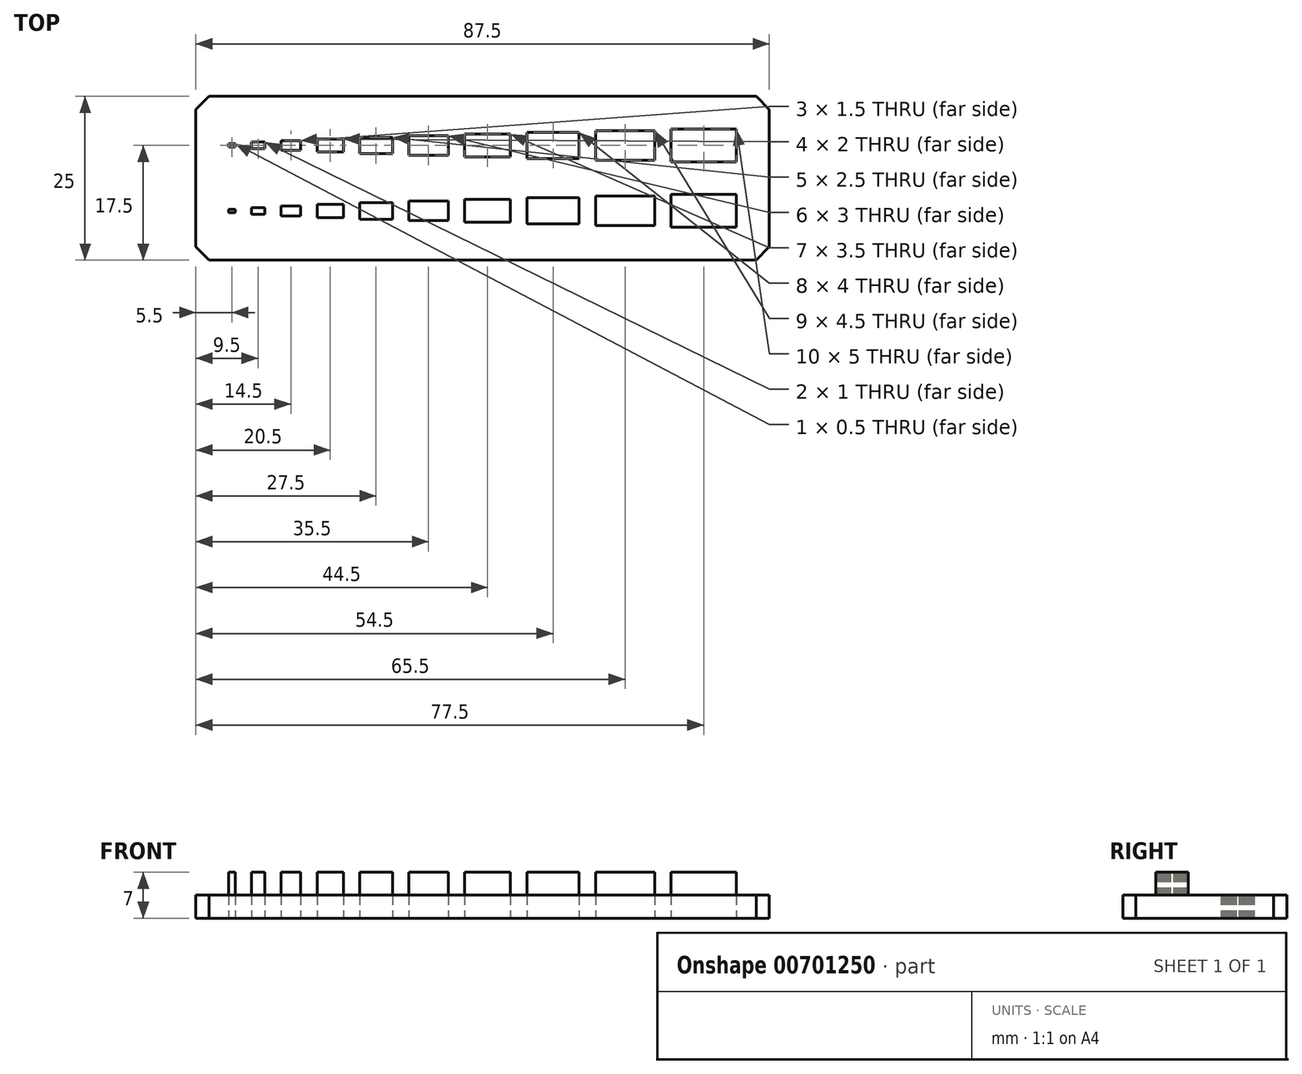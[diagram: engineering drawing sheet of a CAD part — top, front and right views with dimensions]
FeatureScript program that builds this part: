
annotation { "Feature Type Name" : "Feature", "Feature Type Description" : "" }
export const myFeature = defineFeature(function(context is Context, id is Id, definition is map)
    precondition{}
    {
        {
            var Q0;
            Q0=qCreatedBy(makeId("Top.planeOp"),FACE);
            var sketch = newSketch(context, id + "F0", { "sketchPlane" : qUnion([Q0])});
            skLineSegment(sketch, "E0.bottom", {"start": v(-37.75, 5.25) * mm, "end": v(-38.25, 5.25) * mm});
            skLineSegment(sketch, "E0.top", {"start": v(-37.75, 4.75) * mm, "end": v(-38.75, 4.75) * mm});
            skLineSegment(sketch, "E0.left", {"start": v(-37.75, 5.25) * mm, "end": v(-37.75, 4.75) * mm});
            skLineSegment(sketch, "E0.right", {"start": v(-38.75, 5.25) * mm, "end": v(-38.75, 4.75) * mm});
            skPoint(sketch, "E0.middle", {"position": v(-38.25, 5) * mm});
            skPoint(sketch, "E1", {"position": v(-38.25, 5.25) * mm});
            skLineSegment(sketch, "E2", {"start": v(-38.25, 5.25) * mm, "end": v(-38.75, 5.25) * mm});
            skLineSegment(sketch, "E3.bottom", {"start": v(-33.25, 5.5) * mm, "end": v(-34.25, 5.5) * mm});
            skLineSegment(sketch, "E3.top", {"start": v(-33.25, 4.5) * mm, "end": v(-35.25, 4.5) * mm});
            skLineSegment(sketch, "E3.left", {"start": v(-33.25, 5.5) * mm, "end": v(-33.25, 4.5) * mm});
            skLineSegment(sketch, "E3.right", {"start": v(-35.25, 5.5) * mm, "end": v(-35.25, 4.5) * mm});
            skPoint(sketch, "E3.middle", {"position": v(-34.25, 5) * mm});
            skLineSegment(sketch, "E4", {"start": v(-34.25, 5.5) * mm, "end": v(-35.25, 5.5) * mm});
            skLineSegment(sketch, "E5", {"start": v(-37.75, 5) * mm, "end": v(-35.25, 5) * mm, "construction": true});
            skLineSegment(sketch, "E6", {"start": v(-33.25, 5) * mm, "end": v(-30.75, 5) * mm, "construction": true});
            skLineSegment(sketch, "E7.bottom", {"start": v(-30.75, 5.75) * mm, "end": v(-29.25, 5.75) * mm});
            skLineSegment(sketch, "E7.top", {"start": v(-30.75, 4.25) * mm, "end": v(-27.75, 4.25) * mm});
            skLineSegment(sketch, "E7.left", {"start": v(-30.75, 5.75) * mm, "end": v(-30.75, 4.25) * mm});
            skLineSegment(sketch, "E7.right", {"start": v(-27.75, 5.75) * mm, "end": v(-27.75, 4.25) * mm});
            skPoint(sketch, "E7.middle", {"position": v(-29.25, 5) * mm});
            skLineSegment(sketch, "E8", {"start": v(-29.25, 5.75) * mm, "end": v(-27.75, 5.75) * mm});
            skLineSegment(sketch, "E9", {"start": v(-27.75, 5) * mm, "end": v(-25.25, 5) * mm, "construction": true});
            skLineSegment(sketch, "E10.bottom", {"start": v(-25.25, 6) * mm, "end": v(-23.25, 6) * mm});
            skLineSegment(sketch, "E10.top", {"start": v(-25.25, 4) * mm, "end": v(-21.25, 4) * mm});
            skLineSegment(sketch, "E10.left", {"start": v(-25.25, 6) * mm, "end": v(-25.25, 4) * mm});
            skLineSegment(sketch, "E10.right", {"start": v(-21.25, 6) * mm, "end": v(-21.25, 4) * mm});
            skPoint(sketch, "E10.middle", {"position": v(-23.25, 5) * mm});
            skLineSegment(sketch, "E11", {"start": v(-23.25, 6) * mm, "end": v(-21.25, 6) * mm});
            skLineSegment(sketch, "E12", {"start": v(-21.25, 5) * mm, "end": v(-18.75, 5) * mm, "construction": true});
            skLineSegment(sketch, "E13.bottom", {"start": v(-18.75, 6.25) * mm, "end": v(-16.25, 6.25) * mm});
            skLineSegment(sketch, "E13.top", {"start": v(-18.75, 3.75) * mm, "end": v(-13.75, 3.75) * mm});
            skLineSegment(sketch, "E13.left", {"start": v(-18.75, 6.25) * mm, "end": v(-18.75, 3.75) * mm});
            skLineSegment(sketch, "E13.right", {"start": v(-13.75, 6.25) * mm, "end": v(-13.75, 3.75) * mm});
            skPoint(sketch, "E13.middle", {"position": v(-16.25, 5) * mm});
            skLineSegment(sketch, "E14", {"start": v(-16.25, 6.25) * mm, "end": v(-13.75, 6.25) * mm});
            skLineSegment(sketch, "E15", {"start": v(-13.75, 5) * mm, "end": v(-11.25, 5) * mm, "construction": true});
            skPoint(sketch, "E15.startSnap0", {"position": v(-13.75, 5) * mm});
            skLineSegment(sketch, "E16.bottom", {"start": v(-11.25, 6.5) * mm, "end": v(-8.25, 6.5) * mm});
            skLineSegment(sketch, "E16.top", {"start": v(-11.25, 3.5) * mm, "end": v(-5.25, 3.5) * mm});
            skLineSegment(sketch, "E16.left", {"start": v(-11.25, 6.5) * mm, "end": v(-11.25, 3.5) * mm});
            skLineSegment(sketch, "E16.right", {"start": v(-5.25, 6.5) * mm, "end": v(-5.25, 3.5) * mm});
            skPoint(sketch, "E16.middle", {"position": v(-8.25, 5) * mm});
            skLineSegment(sketch, "E17", {"start": v(-8.25, 6.5) * mm, "end": v(-5.25, 6.5) * mm});
            skLineSegment(sketch, "E18", {"start": v(-5.25, 5) * mm, "end": v(-2.75, 5) * mm, "construction": true});
            skLineSegment(sketch, "E19.bottom", {"start": v(-2.75, 6.75) * mm, "end": v(0.75, 6.75) * mm});
            skLineSegment(sketch, "E19.top", {"start": v(-2.75, 3.25) * mm, "end": v(4.25, 3.25) * mm});
            skLineSegment(sketch, "E19.left", {"start": v(-2.75, 6.75) * mm, "end": v(-2.75, 3.25) * mm});
            skLineSegment(sketch, "E19.right", {"start": v(4.25, 6.75) * mm, "end": v(4.25, 3.25) * mm});
            skPoint(sketch, "E19.middle", {"position": v(0.75, 5) * mm});
            skLineSegment(sketch, "E20", {"start": v(0.75, 6.75) * mm, "end": v(4.25, 6.75) * mm});
            skLineSegment(sketch, "E21", {"start": v(4.25, 5) * mm, "end": v(6.75, 5) * mm, "construction": true});
            skLineSegment(sketch, "E22.bottom", {"start": v(6.75, 7) * mm, "end": v(10.75, 7) * mm});
            skLineSegment(sketch, "E22.top", {"start": v(6.75, 3) * mm, "end": v(14.75, 3) * mm});
            skLineSegment(sketch, "E22.left", {"start": v(6.75, 7) * mm, "end": v(6.75, 3) * mm});
            skLineSegment(sketch, "E22.right", {"start": v(14.75, 7) * mm, "end": v(14.75, 3) * mm});
            skPoint(sketch, "E22.middle", {"position": v(10.75, 5) * mm});
            skLineSegment(sketch, "E23", {"start": v(10.75, 7) * mm, "end": v(14.75, 7) * mm});
            skLineSegment(sketch, "E24", {"start": v(14.75, 5) * mm, "end": v(17.25, 5) * mm, "construction": true});
            skLineSegment(sketch, "E25.bottom", {"start": v(17.25, 7.25) * mm, "end": v(21.75, 7.25) * mm});
            skLineSegment(sketch, "E25.top", {"start": v(17.25, 2.75) * mm, "end": v(26.25, 2.75) * mm});
            skLineSegment(sketch, "E25.left", {"start": v(17.25, 7.25) * mm, "end": v(17.25, 2.75) * mm});
            skLineSegment(sketch, "E25.right", {"start": v(26.25, 7.25) * mm, "end": v(26.25, 2.75) * mm});
            skPoint(sketch, "E25.middle", {"position": v(21.75, 5) * mm});
            skLineSegment(sketch, "E26", {"start": v(21.75, 7.25) * mm, "end": v(26.25, 7.25) * mm});
            skLineSegment(sketch, "E27", {"start": v(26.25, 5) * mm, "end": v(28.75, 5) * mm, "construction": true});
            skLineSegment(sketch, "E28.bottom", {"start": v(28.75, 7.5) * mm, "end": v(33.75, 7.5) * mm});
            skLineSegment(sketch, "E28.top", {"start": v(28.75, 2.5) * mm, "end": v(38.75, 2.5) * mm});
            skLineSegment(sketch, "E28.left", {"start": v(28.75, 7.5) * mm, "end": v(28.75, 2.5) * mm});
            skLineSegment(sketch, "E28.right", {"start": v(38.75, 7.5) * mm, "end": v(38.75, 2.5) * mm});
            skPoint(sketch, "E28.middle", {"position": v(33.75, 5) * mm});
            skLineSegment(sketch, "E29", {"start": v(33.75, 7.5) * mm, "end": v(38.75, 7.5) * mm});
            skLineSegment(sketch, "E30", {"start": v(38.75, 5) * mm, "end": v(43.75, 5) * mm, "construction": true});
            skLineSegment(sketch, "E31", {"start": v(-38.75, 5) * mm, "end": v(-43.75, 5) * mm, "construction": true});
            skLineSegment(sketch, "E32.bottom", {"start": v(43.75, 12.5) * mm, "end": v(-43.75, 12.5) * mm});
            skLineSegment(sketch, "E32.top", {"start": v(43.75, -12.5) * mm, "end": v(-43.75, -12.5) * mm});
            skLineSegment(sketch, "E32.left", {"start": v(43.75, 12.5) * mm, "end": v(43.75, -12.5) * mm});
            skLineSegment(sketch, "E32.right", {"start": v(-43.75, 12.5) * mm, "end": v(-43.75, -12.5) * mm});
            skPoint(sketch, "E32.middle", {"position": v(0, 0) * mm});
            skLineSegment(sketch, "E33", {"start": v(0, 0) * mm, "end": v(15.69, 0) * mm, "construction": true});
            skLineSegment(sketch, "E34.MirrorCS", {"start": v(-11.25, -6.5) * mm, "end": v(-11.25, -3.5) * mm});
            skLineSegment(sketch, "E35.MirrorCS", {"start": v(-13.75, -6.25) * mm, "end": v(-13.75, -3.75) * mm});
            skLineSegment(sketch, "E36.MirrorCS", {"start": v(-5.25, -6.5) * mm, "end": v(-5.25, -3.5) * mm});
            skLineSegment(sketch, "E37.MirrorCS", {"start": v(-11.25, -3.5) * mm, "end": v(-5.25, -3.5) * mm});
            skLineSegment(sketch, "E38.MirrorCS", {"start": v(-2.75, -6.75) * mm, "end": v(-2.75, -3.25) * mm});
            skLineSegment(sketch, "E39.MirrorCS", {"start": v(4.25, -6.75) * mm, "end": v(4.25, -3.25) * mm});
            skLineSegment(sketch, "E40.MirrorCS", {"start": v(28.75, -2.5) * mm, "end": v(38.75, -2.5) * mm});
            skLineSegment(sketch, "E41.MirrorCS", {"start": v(26.25, -7.25) * mm, "end": v(26.25, -2.75) * mm});
            skLineSegment(sketch, "E42.MirrorCS", {"start": v(-2.75, -3.25) * mm, "end": v(4.25, -3.25) * mm});
            skLineSegment(sketch, "E43.MirrorCS", {"start": v(28.75, -7.5) * mm, "end": v(28.75, -2.5) * mm});
            skLineSegment(sketch, "E44.MirrorCS", {"start": v(6.75, -3) * mm, "end": v(14.75, -3) * mm});
            skLineSegment(sketch, "E45.MirrorCS", {"start": v(17.25, -2.75) * mm, "end": v(26.25, -2.75) * mm});
            skLineSegment(sketch, "E46.MirrorCS", {"start": v(14.75, -7) * mm, "end": v(14.75, -3) * mm});
            skLineSegment(sketch, "E47.MirrorCS", {"start": v(38.75, -7.5) * mm, "end": v(38.75, -2.5) * mm});
            skLineSegment(sketch, "E48.MirrorCS", {"start": v(6.75, -7) * mm, "end": v(6.75, -3) * mm});
            skLineSegment(sketch, "E49.MirrorCS", {"start": v(17.25, -7.25) * mm, "end": v(17.25, -2.75) * mm});
            skLineSegment(sketch, "E50.MirrorCS", {"start": v(-30.75, -5.75) * mm, "end": v(-30.75, -4.25) * mm});
            skLineSegment(sketch, "E51.MirrorCS", {"start": v(-33.25, -5.5) * mm, "end": v(-33.25, -4.5) * mm});
            skLineSegment(sketch, "E52.MirrorCS", {"start": v(-27.75, -5.75) * mm, "end": v(-27.75, -4.25) * mm});
            skLineSegment(sketch, "E53.MirrorCS", {"start": v(-35.25, -5.5) * mm, "end": v(-35.25, -4.5) * mm});
            skLineSegment(sketch, "E54.MirrorCS", {"start": v(-30.75, -4.25) * mm, "end": v(-27.75, -4.25) * mm});
            skLineSegment(sketch, "E55.MirrorCS", {"start": v(-25.25, -6) * mm, "end": v(-25.25, -4) * mm});
            skLineSegment(sketch, "E56.MirrorCS", {"start": v(-18.75, -6.25) * mm, "end": v(-18.75, -3.75) * mm});
            skLineSegment(sketch, "E57.MirrorCS", {"start": v(-18.75, -3.75) * mm, "end": v(-13.75, -3.75) * mm});
            skLineSegment(sketch, "E58.MirrorCS", {"start": v(-33.25, -4.5) * mm, "end": v(-35.25, -4.5) * mm});
            skLineSegment(sketch, "E59.MirrorCS", {"start": v(-25.25, -4) * mm, "end": v(-21.25, -4) * mm});
            skLineSegment(sketch, "E60.MirrorCS", {"start": v(-21.25, -6) * mm, "end": v(-21.25, -4) * mm});
            skLineSegment(sketch, "E61.MirrorCS", {"start": v(-38.75, -5.25) * mm, "end": v(-38.75, -4.75) * mm});
            skLineSegment(sketch, "E62.MirrorCS", {"start": v(-37.75, -4.75) * mm, "end": v(-38.75, -4.75) * mm});
            skLineSegment(sketch, "E63.MirrorCS", {"start": v(-37.75, -5.25) * mm, "end": v(-37.75, -4.75) * mm});
            skLineSegment(sketch, "E64", {"start": v(-38.75, -5.25) * mm, "end": v(-37.75, -5.25) * mm});
            skLineSegment(sketch, "E65", {"start": v(-35.25, -5.5) * mm, "end": v(-33.25, -5.5) * mm});
            skLineSegment(sketch, "E66", {"start": v(-30.75, -5.75) * mm, "end": v(-27.75, -5.75) * mm});
            skLineSegment(sketch, "E67", {"start": v(-25.25, -6) * mm, "end": v(-21.25, -6) * mm});
            skLineSegment(sketch, "E68", {"start": v(-18.75, -6.25) * mm, "end": v(-13.75, -6.25) * mm});
            skLineSegment(sketch, "E69", {"start": v(-11.25, -6.5) * mm, "end": v(-5.25, -6.5) * mm});
            skLineSegment(sketch, "E70", {"start": v(-2.75, -6.75) * mm, "end": v(4.25, -6.75) * mm});
            skLineSegment(sketch, "E71", {"start": v(6.75, -7) * mm, "end": v(14.75, -7) * mm});
            skLineSegment(sketch, "E72", {"start": v(17.25, -7.25) * mm, "end": v(26.25, -7.25) * mm});
            skLineSegment(sketch, "E73", {"start": v(28.75, -7.5) * mm, "end": v(38.75, -7.5) * mm});
            skLineSegment(sketch, "E74", {"start": v(33.75, 7.5) * mm, "end": v(33.75, 12.5) * mm, "construction": true});
            skSolve(sketch);
        }
        {
            var Q0;
            Q0=qSketchRegion(id+"F0",true);
            extrude(context, id + "F1", {"entities" : qUnion([Q0]), "depth" : 3.5 * mm, "offsetDistance" : 25 * mm});
        }
        {
            var Q0;
            Q0=makeQuery(id+"F0.imprint","IMPRINT",FACE,{"disambiguationData":[TD([[makeQuery(id+"F0.imprint","IMPRINT",EDGE,{"derivedFrom":sQuery(id+"F0.wireOp",EDGE,"E61.MirrorCS")}),-1.0]])]});
            var Q1;
            Q1=makeQuery(id+"F0.imprint","IMPRINT",FACE,{"disambiguationData":[TD([[makeQuery(id+"F0.imprint","IMPRINT",EDGE,{"derivedFrom":sQuery(id+"F0.wireOp",EDGE,"E51.MirrorCS")}),1.0]])]});
            var Q2;
            Q2=makeQuery(id+"F0.imprint","IMPRINT",FACE,{"disambiguationData":[TD([[makeQuery(id+"F0.imprint","IMPRINT",EDGE,{"derivedFrom":sQuery(id+"F0.wireOp",EDGE,"E50.MirrorCS")}),-1.0]])]});
            var Q3;
            Q3=makeQuery(id+"F0.imprint","IMPRINT",FACE,{"disambiguationData":[TD([[makeQuery(id+"F0.imprint","IMPRINT",EDGE,{"derivedFrom":sQuery(id+"F0.wireOp",EDGE,"E55.MirrorCS")}),-1.0]])]});
            var Q4;
            Q4=makeQuery(id+"F0.imprint","IMPRINT",FACE,{"disambiguationData":[TD([[makeQuery(id+"F0.imprint","IMPRINT",EDGE,{"derivedFrom":sQuery(id+"F0.wireOp",EDGE,"E35.MirrorCS")}),1.0]])]});
            var Q5;
            Q5=makeQuery(id+"F0.imprint","IMPRINT",FACE,{"disambiguationData":[TD([[makeQuery(id+"F0.imprint","IMPRINT",EDGE,{"derivedFrom":sQuery(id+"F0.wireOp",EDGE,"E34.MirrorCS")}),-1.0]])]});
            var Q6;
            Q6=makeQuery(id+"F0.imprint","IMPRINT",FACE,{"disambiguationData":[TD([[makeQuery(id+"F0.imprint","IMPRINT",EDGE,{"derivedFrom":sQuery(id+"F0.wireOp",EDGE,"E38.MirrorCS")}),-1.0]])]});
            var Q7;
            Q7=makeQuery(id+"F0.imprint","IMPRINT",FACE,{"disambiguationData":[TD([[makeQuery(id+"F0.imprint","IMPRINT",EDGE,{"derivedFrom":sQuery(id+"F0.wireOp",EDGE,"E44.MirrorCS")}),-1.0]])]});
            var Q8;
            Q8=makeQuery(id+"F0.imprint","IMPRINT",FACE,{"disambiguationData":[TD([[makeQuery(id+"F0.imprint","IMPRINT",EDGE,{"derivedFrom":sQuery(id+"F0.wireOp",EDGE,"E41.MirrorCS")}),1.0]])]});
            var Q9;
            Q9=makeQuery(id+"F0.imprint","IMPRINT",FACE,{"disambiguationData":[TD([[makeQuery(id+"F0.imprint","IMPRINT",EDGE,{"derivedFrom":sQuery(id+"F0.wireOp",EDGE,"E40.MirrorCS")}),-1.0]])]});
            var Q10;
            Q10=makeQuery(id+"F1.opExtrude","CAP_FACE",FACE,{"disambiguationData":[OSD([sQuery(id+"F0.wireOp",EDGE,"E0.bottom"),sQuery(id+"F0.wireOp",EDGE,"E0.top"),sQuery(id+"F0.wireOp",EDGE,"E0.left"),sQuery(id+"F0.wireOp",EDGE,"E0.right"),sQuery(id+"F0.wireOp",EDGE,"E2"),sQuery(id+"F0.wireOp",EDGE,"E3.bottom"),sQuery(id+"F0.wireOp",EDGE,"E3.top"),sQuery(id+"F0.wireOp",EDGE,"E3.left"),sQuery(id+"F0.wireOp",EDGE,"E3.right"),sQuery(id+"F0.wireOp",EDGE,"E4"),sQuery(id+"F0.wireOp",EDGE,"E7.bottom"),sQuery(id+"F0.wireOp",EDGE,"E7.top"),sQuery(id+"F0.wireOp",EDGE,"E7.left"),sQuery(id+"F0.wireOp",EDGE,"E7.right"),sQuery(id+"F0.wireOp",EDGE,"E8"),sQuery(id+"F0.wireOp",EDGE,"E10.bottom"),sQuery(id+"F0.wireOp",EDGE,"E10.top"),sQuery(id+"F0.wireOp",EDGE,"E10.left"),sQuery(id+"F0.wireOp",EDGE,"E10.right"),sQuery(id+"F0.wireOp",EDGE,"E11"),sQuery(id+"F0.wireOp",EDGE,"E13.bottom"),sQuery(id+"F0.wireOp",EDGE,"E13.top"),sQuery(id+"F0.wireOp",EDGE,"E13.left"),sQuery(id+"F0.wireOp",EDGE,"E13.right"),sQuery(id+"F0.wireOp",EDGE,"E14"),sQuery(id+"F0.wireOp",EDGE,"E16.bottom"),sQuery(id+"F0.wireOp",EDGE,"E16.top"),sQuery(id+"F0.wireOp",EDGE,"E16.left"),sQuery(id+"F0.wireOp",EDGE,"E16.right"),sQuery(id+"F0.wireOp",EDGE,"E17"),sQuery(id+"F0.wireOp",EDGE,"E19.bottom"),sQuery(id+"F0.wireOp",EDGE,"E19.top"),sQuery(id+"F0.wireOp",EDGE,"E19.left"),sQuery(id+"F0.wireOp",EDGE,"E19.right"),sQuery(id+"F0.wireOp",EDGE,"E20"),sQuery(id+"F0.wireOp",EDGE,"E22.bottom"),sQuery(id+"F0.wireOp",EDGE,"E22.top"),sQuery(id+"F0.wireOp",EDGE,"E22.left"),sQuery(id+"F0.wireOp",EDGE,"E22.right"),sQuery(id+"F0.wireOp",EDGE,"E23"),sQuery(id+"F0.wireOp",EDGE,"E25.bottom"),sQuery(id+"F0.wireOp",EDGE,"E25.top"),sQuery(id+"F0.wireOp",EDGE,"E25.left"),sQuery(id+"F0.wireOp",EDGE,"E25.right"),sQuery(id+"F0.wireOp",EDGE,"E26"),sQuery(id+"F0.wireOp",EDGE,"E28.bottom"),sQuery(id+"F0.wireOp",EDGE,"E28.top"),sQuery(id+"F0.wireOp",EDGE,"E28.left"),sQuery(id+"F0.wireOp",EDGE,"E28.right"),sQuery(id+"F0.wireOp",EDGE,"E29"),sQuery(id+"F0.wireOp",EDGE,"E32.bottom"),sQuery(id+"F0.wireOp",EDGE,"E32.top"),sQuery(id+"F0.wireOp",EDGE,"E32.left"),sQuery(id+"F0.wireOp",EDGE,"E32.right"),sQuery(id+"F0.wireOp",EDGE,"E34.MirrorCS"),sQuery(id+"F0.wireOp",EDGE,"E35.MirrorCS"),sQuery(id+"F0.wireOp",EDGE,"E36.MirrorCS"),sQuery(id+"F0.wireOp",EDGE,"E37.MirrorCS"),sQuery(id+"F0.wireOp",EDGE,"E38.MirrorCS"),sQuery(id+"F0.wireOp",EDGE,"E39.MirrorCS"),sQuery(id+"F0.wireOp",EDGE,"E40.MirrorCS"),sQuery(id+"F0.wireOp",EDGE,"E41.MirrorCS"),sQuery(id+"F0.wireOp",EDGE,"E42.MirrorCS"),sQuery(id+"F0.wireOp",EDGE,"E43.MirrorCS"),sQuery(id+"F0.wireOp",EDGE,"E44.MirrorCS"),sQuery(id+"F0.wireOp",EDGE,"E45.MirrorCS"),sQuery(id+"F0.wireOp",EDGE,"E46.MirrorCS"),sQuery(id+"F0.wireOp",EDGE,"E47.MirrorCS"),sQuery(id+"F0.wireOp",EDGE,"E48.MirrorCS"),sQuery(id+"F0.wireOp",EDGE,"E49.MirrorCS"),sQuery(id+"F0.wireOp",EDGE,"E50.MirrorCS"),sQuery(id+"F0.wireOp",EDGE,"E51.MirrorCS"),sQuery(id+"F0.wireOp",EDGE,"E52.MirrorCS"),sQuery(id+"F0.wireOp",EDGE,"E53.MirrorCS"),sQuery(id+"F0.wireOp",EDGE,"E54.MirrorCS"),sQuery(id+"F0.wireOp",EDGE,"E55.MirrorCS"),sQuery(id+"F0.wireOp",EDGE,"E56.MirrorCS"),sQuery(id+"F0.wireOp",EDGE,"E57.MirrorCS"),sQuery(id+"F0.wireOp",EDGE,"E58.MirrorCS"),sQuery(id+"F0.wireOp",EDGE,"E59.MirrorCS"),sQuery(id+"F0.wireOp",EDGE,"E60.MirrorCS"),sQuery(id+"F0.wireOp",EDGE,"E61.MirrorCS"),sQuery(id+"F0.wireOp",EDGE,"E62.MirrorCS"),sQuery(id+"F0.wireOp",EDGE,"E63.MirrorCS"),sQuery(id+"F0.wireOp",EDGE,"E64"),sQuery(id+"F0.wireOp",EDGE,"E65"),sQuery(id+"F0.wireOp",EDGE,"E66"),sQuery(id+"F0.wireOp",EDGE,"E67"),sQuery(id+"F0.wireOp",EDGE,"E68"),sQuery(id+"F0.wireOp",EDGE,"E69"),sQuery(id+"F0.wireOp",EDGE,"E70"),sQuery(id+"F0.wireOp",EDGE,"E71"),sQuery(id+"F0.wireOp",EDGE,"E72"),sQuery(id+"F0.wireOp",EDGE,"E73")])],"isStart":false});
            extrude(context, id + "F2", {"entities" : qUnion([Q0, Q1, Q2, Q3, Q4, Q5, Q6, Q7, Q8, Q9]), "operationType" : NewBodyOperationType.ADD, "endBound" : BoundingType.UP_TO_SURFACE, "depth" : 25 * mm, "endBoundEntityFace" : qUnion([Q10]), "hasOffset" : true, "offsetDistance" : 3.5 * mm, "offsetOppositeDirection" : true});
        }
        {
            var Q0;
            Q0=makeQuery(id+"F1.opExtrude","SWEPT_EDGE",EDGE,{"disambiguationData":[OSD([sQuery(id+"F0.wireOp",EDGE,"E32.top"),sQuery(id+"F0.wireOp",EDGE,"E32.right")])]});
            var Q1;
            Q1=makeQuery(id+"F1.opExtrude","SWEPT_EDGE",EDGE,{"disambiguationData":[OSD([sQuery(id+"F0.wireOp",EDGE,"E32.top"),sQuery(id+"F0.wireOp",EDGE,"E32.left")])]});
            var Q2;
            Q2=makeQuery(id+"F1.opExtrude","SWEPT_EDGE",EDGE,{"disambiguationData":[OSD([sQuery(id+"F0.wireOp",EDGE,"E32.bottom"),sQuery(id+"F0.wireOp",EDGE,"E32.left")])]});
            var Q3;
            Q3=makeQuery(id+"F1.opExtrude","SWEPT_EDGE",EDGE,{"disambiguationData":[OSD([sQuery(id+"F0.wireOp",EDGE,"E32.bottom"),sQuery(id+"F0.wireOp",EDGE,"E32.right")])]});
            chamfer(context, id + "F3", {"entities" : qUnion([Q0, Q1, Q2, Q3]), "width" : 2 * mm, "tangentPropagation" : true});
        }
    });
